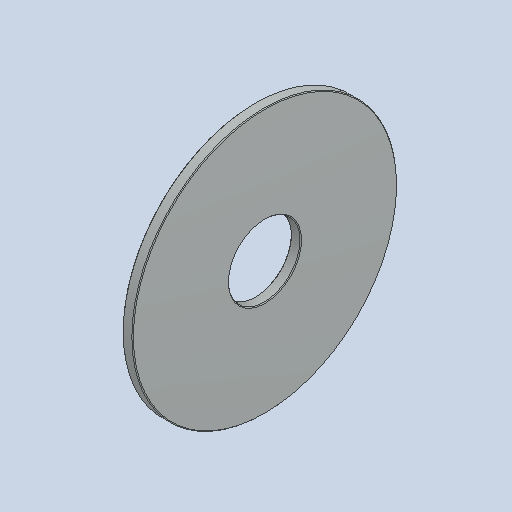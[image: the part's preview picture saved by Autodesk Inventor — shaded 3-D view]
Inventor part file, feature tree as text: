
AUTODESK INVENTOR PART (.ipt)
format: ipt  version: 2024.1 (Build 281209000, 209)  size: 128,000 bytes
history: native  units: in
note: dims shown in document units (in); Inventor stores cm internally (conversion verified against a paired STEP export)
features: chamfer x1
ambient origin geometry x8: Origin, YZ Plane, XZ Plane, XY Plane, X Axis, Y Axis, Z Axis, Center Point
bodies: Solid1 (feature_tree)
feature tree (1):
  chamfer  "Chamfer2"  [1 undecoded]
note: 1 required parameter value undecoded (feature->parameter linkage not recoverable at this tier; creation-order binding heuristic only, values carry confidence <= 0.55)
